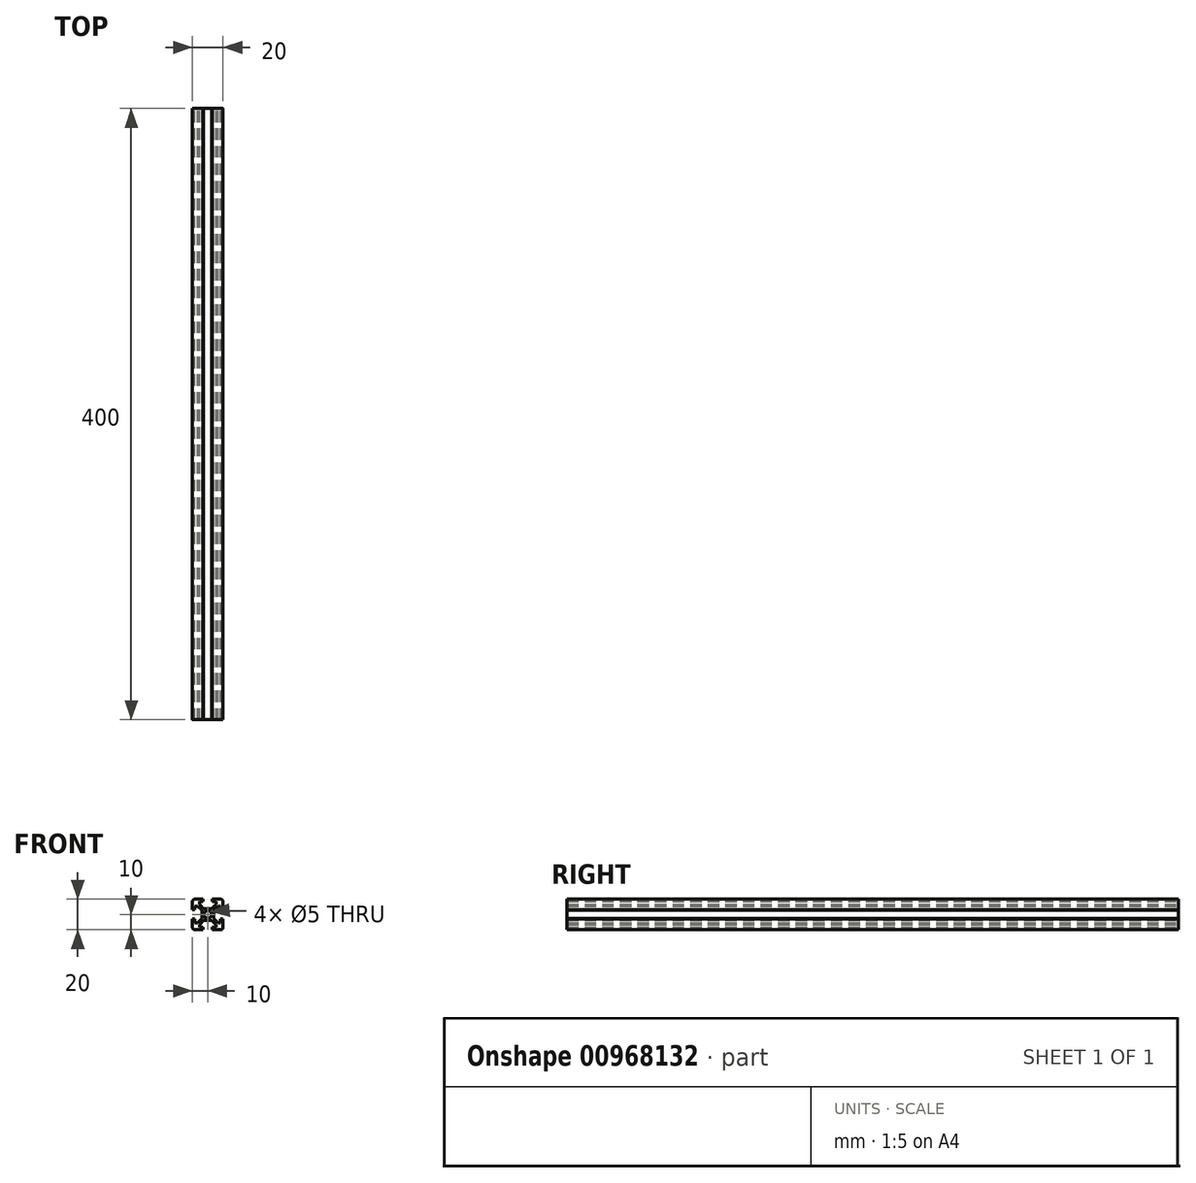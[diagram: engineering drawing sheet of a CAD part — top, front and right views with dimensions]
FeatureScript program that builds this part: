
annotation { "Feature Type Name" : "Feature", "Feature Type Description" : "" }
export const myFeature = defineFeature(function(context is Context, id is Id, definition is map)
    precondition{}
    {
        {
            var Q0;
            Q0=qCreatedBy(makeId("Front.planeOp"),FACE);
            var sketch = newSketch(context, id + "F0", { "sketchPlane" : qUnion([Q0])});
            skCircle(sketch, "E0", {"center": v(0, 0) * mm, "radius": 2.5 * mm});
            skLineSegment(sketch, "E1.bottom", {"start": v(3.75, -3.75) * mm, "end": v(-3.75, -3.75) * mm});
            skLineSegment(sketch, "E1.top", {"start": v(3.75, 3.75) * mm, "end": v(-2.69, 3.75) * mm});
            skLineSegment(sketch, "E1.left", {"start": v(3.75, -3.75) * mm, "end": v(3.75, 3.75) * mm});
            skLineSegment(sketch, "E1.right", {"start": v(-3.75, -3.75) * mm, "end": v(-3.75, 2.69) * mm});
            skLineSegment(sketch, "E2.top", {"start": v(-8.4, 5.5) * mm, "end": v(-6.56, 5.5) * mm});
            skLineSegment(sketch, "E2.right", {"start": v(-5.5, 8.4) * mm, "end": v(-5.5, 6.56) * mm});
            skLineSegment(sketch, "E3.top", {"start": v(-5.5, 8.4) * mm, "end": v(-3, 8.4) * mm});
            skLineSegment(sketch, "E3.left", {"start": v(-10, 8.4) * mm, "end": v(-10, 8.4) * mm});
            skLineSegment(sketch, "E4.bottom", {"start": v(-8.4, 10) * mm, "end": v(-8.4, 10) * mm});
            skLineSegment(sketch, "E4.top", {"start": v(-10, 3) * mm, "end": v(-8.4, 3) * mm});
            skLineSegment(sketch, "E5.trimOffspring", {"start": v(-8.4, 5.5) * mm, "end": v(-8.4, 3) * mm});
            skPoint(sketch, "E6.orphan", {"position": v(-3.75, 3.75) * mm});
            skPoint(sketch, "E7.1.1", {"position": v(-3.75, -3.75) * mm});
            skPoint(sketch, "E7.2.1", {"position": v(3.75, -3.75) * mm});
            skPoint(sketch, "E7.3.1", {"position": v(3.75, 3.75) * mm});
            skArc(sketch, "E8.filletArc", {"start": v(-8.4, 10) * mm, "mid": v(-9.53, 9.53) * mm, "end": v(-10, 8.4) * mm});
            skPoint(sketch, "E9", {"position": v(-8.4, 10) * mm});
            skPoint(sketch, "E10", {"position": v(-10, 8.4) * mm});
            skLineSegment(sketch, "E11", {"start": v(-8.4, 10) * mm, "end": v(-3, 10) * mm});
            skLineSegment(sketch, "E12", {"start": v(-3, 10) * mm, "end": v(-3, 8.4) * mm});
            skLineSegment(sketch, "E13", {"start": v(-10, 3) * mm, "end": v(-10, 8.4) * mm});
            skLineSegment(sketch, "E14", {"start": v(-5.5, 6.56) * mm, "end": v(-2.69, 3.75) * mm});
            skLineSegment(sketch, "E15", {"start": v(-3.75, 2.69) * mm, "end": v(-6.56, 5.5) * mm});
            skLineSegment(sketch, "E16.1.0", {"start": v(-6.56, -5.5) * mm, "end": v(-3.75, -2.69) * mm});
            skLineSegment(sketch, "E16.1.1", {"start": v(-10, -3) * mm, "end": v(-8.4, -3) * mm});
            skArc(sketch, "E16.1.3", {"start": v(-10, -8.4) * mm, "mid": v(-9.53, -9.53) * mm, "end": v(-8.4, -10) * mm});
            skLineSegment(sketch, "E16.1.4", {"start": v(-3, -10) * mm, "end": v(-8.4, -10) * mm});
            skLineSegment(sketch, "E16.1.5", {"start": v(-8.4, -5.5) * mm, "end": v(-6.56, -5.5) * mm});
            skLineSegment(sketch, "E16.1.6", {"start": v(-10, -8.4) * mm, "end": v(-10, -3) * mm});
            skLineSegment(sketch, "E16.1.7", {"start": v(-5.5, -8.4) * mm, "end": v(-3, -8.4) * mm});
            skLineSegment(sketch, "E16.1.8", {"start": v(-5.5, -8.4) * mm, "end": v(-5.5, -6.56) * mm});
            skLineSegment(sketch, "E16.1.9", {"start": v(-3, -10) * mm, "end": v(-3, -8.4) * mm});
            skLineSegment(sketch, "E16.1.10", {"start": v(-2.69, -3.75) * mm, "end": v(-5.5, -6.56) * mm});
            skLineSegment(sketch, "E16.1.11", {"start": v(-8.4, -5.5) * mm, "end": v(-8.4, -3) * mm});
            skPoint(sketch, "E16.1.12", {"position": v(-8.4, -10) * mm});
            skPoint(sketch, "E16.1.13", {"position": v(-10, -8.4) * mm});
            skLineSegment(sketch, "E16.2.0", {"start": v(5.5, -6.56) * mm, "end": v(2.69, -3.75) * mm});
            skLineSegment(sketch, "E16.2.1", {"start": v(3, -10) * mm, "end": v(3, -8.4) * mm});
            skArc(sketch, "E16.2.3", {"start": v(8.4, -10) * mm, "mid": v(9.53, -9.53) * mm, "end": v(10, -8.4) * mm});
            skLineSegment(sketch, "E16.2.4", {"start": v(10, -3) * mm, "end": v(10, -8.4) * mm});
            skLineSegment(sketch, "E16.2.5", {"start": v(5.5, -8.4) * mm, "end": v(5.5, -6.56) * mm});
            skLineSegment(sketch, "E16.2.6", {"start": v(8.4, -10) * mm, "end": v(3, -10) * mm});
            skLineSegment(sketch, "E16.2.7", {"start": v(8.4, -5.5) * mm, "end": v(8.4, -3) * mm});
            skLineSegment(sketch, "E16.2.8", {"start": v(8.4, -5.5) * mm, "end": v(6.56, -5.5) * mm});
            skLineSegment(sketch, "E16.2.9", {"start": v(10, -3) * mm, "end": v(8.4, -3) * mm});
            skLineSegment(sketch, "E16.2.10", {"start": v(3.75, -2.69) * mm, "end": v(6.56, -5.5) * mm});
            skLineSegment(sketch, "E16.2.11", {"start": v(5.5, -8.4) * mm, "end": v(3, -8.4) * mm});
            skPoint(sketch, "E16.2.12", {"position": v(10, -8.4) * mm});
            skPoint(sketch, "E16.2.13", {"position": v(8.4, -10) * mm});
            skLineSegment(sketch, "E16.3.0", {"start": v(6.56, 5.5) * mm, "end": v(3.75, 2.69) * mm});
            skLineSegment(sketch, "E16.3.1", {"start": v(10, 3) * mm, "end": v(8.4, 3) * mm});
            skArc(sketch, "E16.3.3", {"start": v(10, 8.4) * mm, "mid": v(9.53, 9.53) * mm, "end": v(8.4, 10) * mm});
            skLineSegment(sketch, "E16.3.4", {"start": v(3, 10) * mm, "end": v(8.4, 10) * mm});
            skLineSegment(sketch, "E16.3.5", {"start": v(8.4, 5.5) * mm, "end": v(6.56, 5.5) * mm});
            skLineSegment(sketch, "E16.3.6", {"start": v(10, 8.4) * mm, "end": v(10, 3) * mm});
            skLineSegment(sketch, "E16.3.7", {"start": v(5.5, 8.4) * mm, "end": v(3, 8.4) * mm});
            skLineSegment(sketch, "E16.3.8", {"start": v(5.5, 8.4) * mm, "end": v(5.5, 6.56) * mm});
            skLineSegment(sketch, "E16.3.9", {"start": v(3, 10) * mm, "end": v(3, 8.4) * mm});
            skLineSegment(sketch, "E16.3.10", {"start": v(2.69, 3.75) * mm, "end": v(5.5, 6.56) * mm});
            skLineSegment(sketch, "E16.3.11", {"start": v(8.4, 5.5) * mm, "end": v(8.4, 3) * mm});
            skPoint(sketch, "E16.3.12", {"position": v(8.4, 10) * mm});
            skPoint(sketch, "E16.3.13", {"position": v(10, 8.4) * mm});
            skSolve(sketch);
        }
        {
            var Q0;
            Q0=makeQuery(id+"F0.imprint","IMPRINT",FACE,{"disambiguationData":[TD([[makeQuery(id+"F0.imprint","IMPRINT",EDGE,{"derivedFrom":sQuery(id+"F0.wireOp",EDGE,"E0")}),-1.0]])]});
            var Q1;
            {var subQ4=sQuery(id+"F0.wireOp",EDGE,"E16.3.0");Q1=makeQuery(id+"F0.imprint","IMPRINT",FACE,{"disambiguationData":[TD([[makeQuery(id+"F0.imprint","IMPRINT",EDGE,{"derivedFrom":subQ4}),-1.0]])]});}
            var Q2;
            {var subQ4=sQuery(id+"F0.wireOp",EDGE,"E16.2.0");Q2=makeQuery(id+"F0.imprint","IMPRINT",FACE,{"disambiguationData":[TD([[makeQuery(id+"F0.imprint","IMPRINT",EDGE,{"derivedFrom":subQ4}),-1.0]])]});}
            var Q3;
            {var subQ4=sQuery(id+"F0.wireOp",EDGE,"E16.1.0");Q3=makeQuery(id+"F0.imprint","IMPRINT",FACE,{"disambiguationData":[TD([[makeQuery(id+"F0.imprint","IMPRINT",EDGE,{"derivedFrom":subQ4}),-1.0]])]});}
            extrude(context, id + "F1", {"entities" : qUnion([Q0, Q1, Q2, Q3]), "endBound" : BoundingType.SYMMETRIC, "depth" : 400 * mm, "offsetDistance" : 25 * mm});
        }
    });
